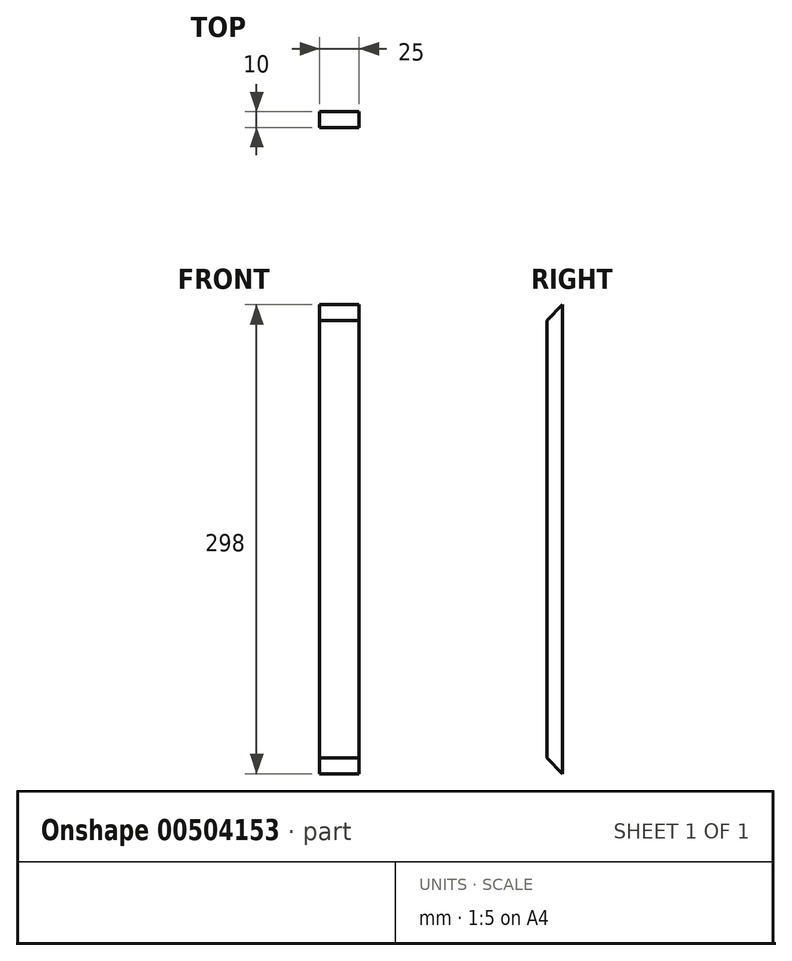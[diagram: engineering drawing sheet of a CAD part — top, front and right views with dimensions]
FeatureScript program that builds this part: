
annotation { "Feature Type Name" : "Feature", "Feature Type Description" : "" }
export const myFeature = defineFeature(function(context is Context, id is Id, definition is map)
    precondition{}
    {
        {
            var Q0;
            Q0=qCreatedBy(makeId("Front.planeOp"),FACE);
            var sketch = newSketch(context, id + "F0", { "sketchPlane" : qUnion([Q0])});
            skLineSegment(sketch, "E0.bottom", {"start": v(12.5, -149) * mm, "end": v(-12.5, -149) * mm});
            skLineSegment(sketch, "E0.top", {"start": v(12.5, 149) * mm, "end": v(-12.5, 149) * mm});
            skLineSegment(sketch, "E0.left", {"start": v(12.5, -149) * mm, "end": v(12.5, 149) * mm});
            skLineSegment(sketch, "E0.right", {"start": v(-12.5, -149) * mm, "end": v(-12.5, 149) * mm});
            skPoint(sketch, "E0.middle", {"position": v(0, 0) * mm});
            skSolve(sketch);
        }
        {
            var Q0;
            Q0=makeQuery(id+"F0.imprint","IMPRINT",FACE,{"disambiguationData":[TD([[makeQuery(id+"F0.imprint","IMPRINT",EDGE,{"derivedFrom":sQuery(id+"F0.wireOp",EDGE,"E0.bottom")}),-1.0]])]});
            extrude(context, id + "F1", {"entities" : qUnion([Q0]), "depth" : 10 * mm, "offsetDistance" : 25 * mm});
        }
        {
            var Q0;
            Q0=makeQuery(id+"F1.opExtrude","CAP_EDGE",EDGE,{"disambiguationData":[OSD([sQuery(id+"F0.wireOp",EDGE,"E0.top")])],"isStart":false});
            var Q1;
            Q1=makeQuery(id+"F1.opExtrude","CAP_EDGE",EDGE,{"disambiguationData":[OSD([sQuery(id+"F0.wireOp",EDGE,"E0.bottom")])],"isStart":false});
            chamfer(context, id + "F2", {"entities" : qUnion([Q0, Q1]), "chamferType" : ChamferType.OFFSET_ANGLE, "width" : 10 * mm, "oppositeDirection" : false, "angle" : 45 * degree, "tangentPropagation" : true});
        }
    });
